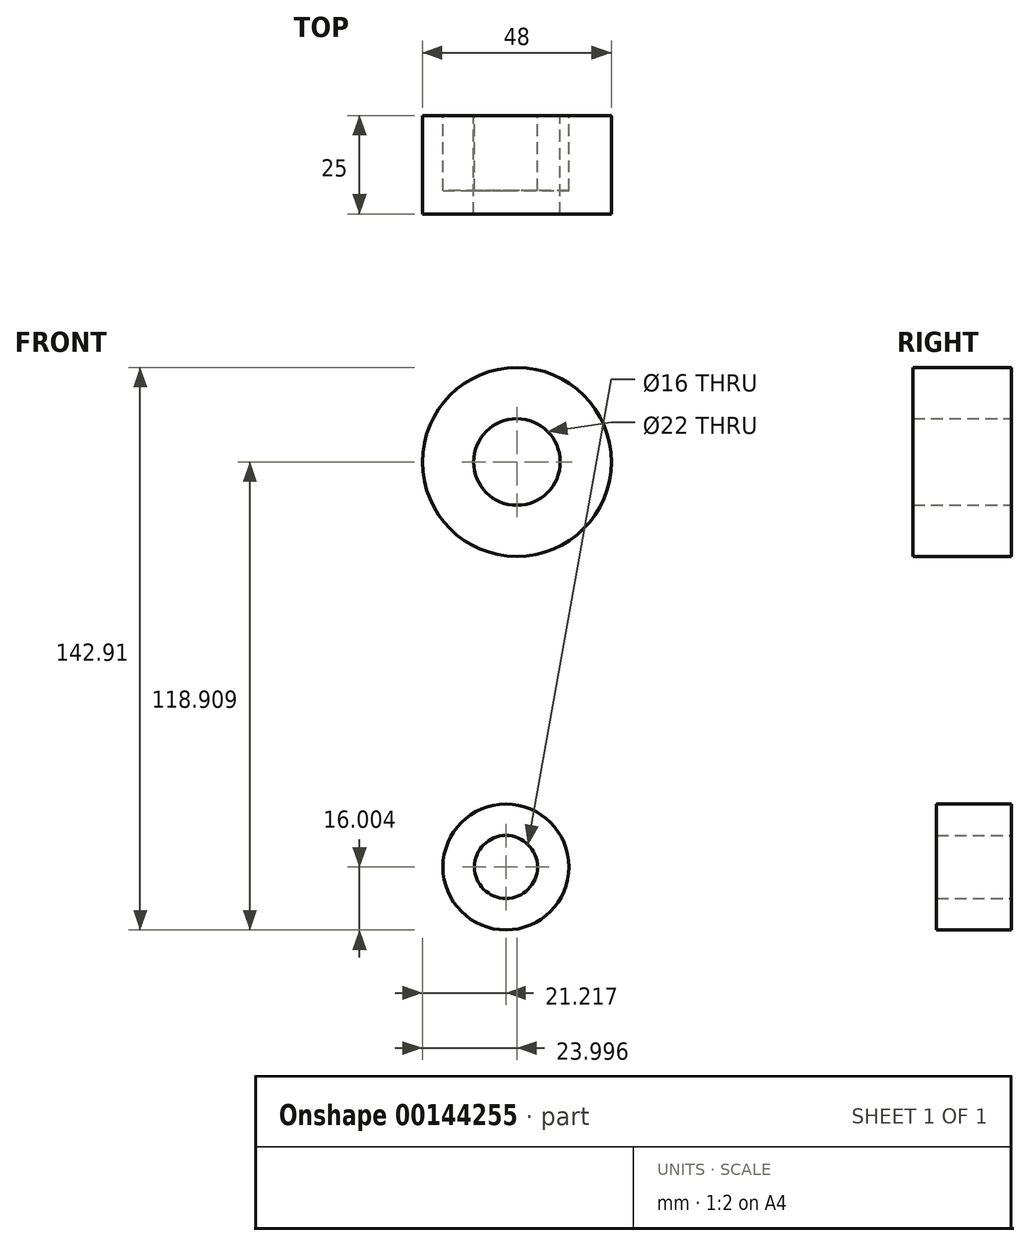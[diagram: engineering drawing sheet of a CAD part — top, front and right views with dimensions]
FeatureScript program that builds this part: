
annotation { "Feature Type Name" : "Feature", "Feature Type Description" : "" }
export const myFeature = defineFeature(function(context is Context, id is Id, definition is map)
    precondition{}
    {
        {
            var Q0;
            Q0=qCreatedBy(makeId("Front.planeOp"),FACE);
            var sketch = newSketch(context, id + "F0", { "sketchPlane" : qUnion([Q0])});
            skCircle(sketch, "E0", {"center": v(-49.97, 44.46) * mm, "radius": 24 * mm});
            skCircle(sketch, "E1", {"center": v(-49.97, 44.46) * mm, "radius": 11 * mm});
            skSolve(sketch);
        }
        {
            var Q0;
            Q0 = qSketchRegion(id + "F0", true);
            extrude(context, id + "F1", {"entities" : qUnion([Q0]), "depth" : 25 * mm});
        }
        {
            var Q0;
            Q0=qCreatedBy(makeId("Front.planeOp"),FACE);
            var sketch = newSketch(context, id + "F2", { "sketchPlane" : qUnion([Q0])});
            skCircle(sketch, "E2", {"center": v(-52.75, -58.45) * mm, "radius": 16 * mm});
            skCircle(sketch, "E3", {"center": v(-52.75, -58.45) * mm, "radius": 8 * mm});
            skSolve(sketch);
        }
        {
            var Q0;
            Q0 = qSketchRegion(id + "F2", true);
            extrude(context, id + "F3", {"entities" : qUnion([Q0]), "depth" : 19 * mm});
        }
        {
            var Q0;
            Q0=sQuery(id+"F0.wireOp",VERTEX,"E0.center");
            var Q1;
            Q1=qCreatedBy(makeId("Top.planeOp"),FACE);
            cPlane(context, id + "F4", {"entities" : qUnion([Q0, Q1]), "cplaneType" : CPlaneType.PLANE_POINT, "offset" : 25 * mm, "width" : 150 * mm, "height" : 150 * mm});
        }
        {
            var Q0;
            Q0=sQuery(id+"F2.wireOp",VERTEX,"E2.center");
            var Q1;
            Q1=qCreatedBy(makeId("Top.planeOp"),FACE);
            cPlane(context, id + "F5", {"entities" : qUnion([Q0, Q1]), "cplaneType" : CPlaneType.PLANE_POINT, "offset" : 25 * mm, "width" : 150 * mm, "height" : 150 * mm});
        }
        {
            var Q0;
            Q0=qCreatedBy(id+"F5.planeOp",FACE);
            var sketch = newSketch(context, id + "F6", { "sketchPlane" : qUnion([Q0])});
            skEllipse(sketch, "E4", {"center": v(-52.75, -9.49) * mm, "majorRadius": 11.77 * mm, "minorRadius": 5.3 * mm, "majorAxis": v(1, 0)});
            skSolve(sketch);
        }
        {
            var Q0;
            Q0=qCreatedBy(id+"F4.planeOp",FACE);
            var sketch = newSketch(context, id + "F7", { "sketchPlane" : qUnion([Q0])});
            skEllipse(sketch, "E5", {"center": v(-52.94, -9.1) * mm, "majorRadius": 14.04 * mm, "minorRadius": 6.06 * mm, "majorAxis": v(1, 0)});
            skSolve(sketch);
        }
        {
            var Q0;
            Q0=makeQuery(id+"F7.imprint","IMPRINT",FACE,{"disambiguationData":[TD([[makeQuery(id+"F7.imprint","IMPRINT",EDGE,{"derivedFrom":sQuery(id+"F7.wireOp",EDGE,"E5")}),1.0]])]});
            var Q1;
            Q1=makeQuery(id+"F6.imprint","IMPRINT",FACE,{"disambiguationData":[TD([[makeQuery(id+"F6.imprint","IMPRINT",EDGE,{"derivedFrom":sQuery(id+"F6.wireOp",EDGE,"E4")}),1.0]])]});
            loft(context, id + "F8", {"sheetProfilesArray" : [{ "sheetProfileEntities" : qUnion([Q0]) }, { "sheetProfileEntities" : qUnion([Q1]) }]});
        }
        {
            var Q0;
            Q0=qCreatedBy(makeId("Front.planeOp"),FACE);
            var sketch = newSketch(context, id + "F9", { "sketchPlane" : qUnion([Q0])});
            skCircle(sketch, "E6.0", {"center": v(-49.97, 44.46) * mm, "radius": 11 * mm});
            skCircle(sketch, "E7.0", {"center": v(-52.75, -58.45) * mm, "radius": 8 * mm});
            skSolve(sketch);
        }
        {
            var Q0;
            Q0 = qSketchRegion(id + "F9", true);
            extrude(context, id + "F10", {"entities" : qUnion([Q0]), "operationType" : NewBodyOperationType.REMOVE, "depth" : 25 * mm});
        }
    });
